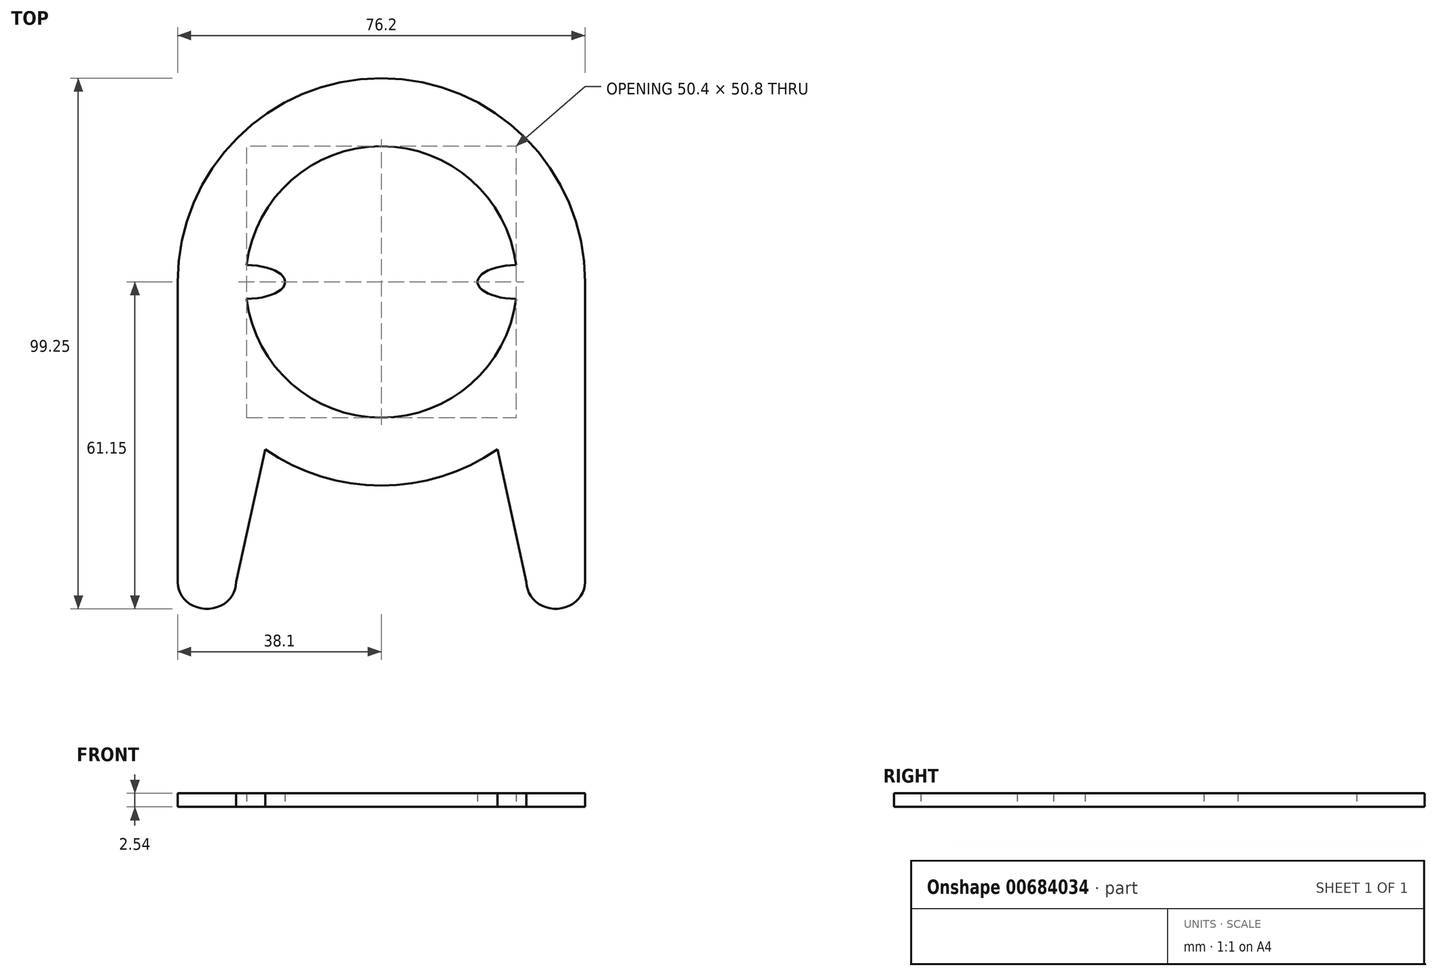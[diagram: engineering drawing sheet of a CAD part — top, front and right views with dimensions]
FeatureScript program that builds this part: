
annotation { "Feature Type Name" : "Feature", "Feature Type Description" : "" }
export const myFeature = defineFeature(function(context is Context, id is Id, definition is map)
    precondition{}
    {
        {
            var Q0;
            Q0=qCreatedBy(makeId("Top.planeOp"),FACE);
            var sketch = newSketch(context, id + "F0", { "sketchPlane" : qUnion([Q0])});
            skCircle(sketch, "E0", {"center": v(0, 0) * mm, "radius": 38.1 * mm});
            skCircle(sketch, "E1", {"center": v(0, 0) * mm, "radius": 25.4 * mm});
            skLineSegment(sketch, "E2", {"start": v(-38.1, 0) * mm, "end": v(-38.1, -56.12) * mm});
            skLineSegment(sketch, "E3", {"start": v(38.1, -56.12) * mm, "end": v(38.1, 0) * mm});
            skLineSegment(sketch, "E4", {"start": v(0, 77.4) * mm, "end": v(0, -99.38) * mm, "construction": true});
            skEllipticalArc(sketch, "E5", {});
            skEllipticalArc(sketch, "E6.MirrorC", {});
            skLineSegment(sketch, "E7", {"start": v(-38.1, -56.12) * mm, "end": v(-27.15, -56.12) * mm});
            skLineSegment(sketch, "E8", {"start": v(-27.15, -56.12) * mm, "end": v(-21.72, -31.3) * mm});
            skEllipticalArc(sketch, "E9", {});
            skLineSegment(sketch, "E10.MirrorCS", {"start": v(27.15, -56.12) * mm, "end": v(21.72, -31.3) * mm});
            skLineSegment(sketch, "E11.MirrorCS", {"start": v(38.1, -56.12) * mm, "end": v(27.15, -56.12) * mm});
            skEllipticalArc(sketch, "E12.MirrorCS", {});
            const initialGuessF0  = {"E5": [-0.0254, 0, -1, 0, 0.0073998064458370184, 0.003175, 1.597702169626156, 4.6854831375534305], "E6.MirrorC": [0.0254, 0, 1, 0, 0.0073998064458370184, 0.003175, 1.5977021696261542, 4.685483137553433], "E9": [-0.032624441894888875, -0.05611676641900889, 0, 1, 0.005029153078794479, 0.005475558105111124, 1.5707963267948966, 4.71238898038469], "E12.MirrorCS": [0.03262444189488892, -0.05611676641900888, 0, 1, 0.005029153078794479, 0.005475558105111124, 1.5707963267948966, 4.71238898038469]};
            skSetInitialGuess(sketch, initialGuessF0);
            skSolve(sketch);
        }
        {
            var Q0;
            Q0 = qSketchRegion(id + "F0", true);
            var Q1;
            {var subQ0=sQuery(id+"F0.wireOp",EDGE,"E5");Q1=makeQuery(id+"F0.imprint","IMPRINT",FACE,{"disambiguationData":[TD([[makeQuery(id+"F0.imprint","IMPRINT",EDGE,{"derivedFrom":subQ0}),1.0]])]});}
            var Q2;
            {var subQ0=sQuery(id+"F0.wireOp",EDGE,"E6.MirrorC");Q2=makeQuery(id+"F0.imprint","IMPRINT",FACE,{"disambiguationData":[TD([[makeQuery(id+"F0.imprint","IMPRINT",EDGE,{"derivedFrom":subQ0}),1.0]])]});}
            extrude(context, id + "F1", {"entities" : qUnion([Q0, Q1, Q2]), "depth" : 2.54 * mm, "offsetDistance" : 25.4 * mm});
        }
    });
